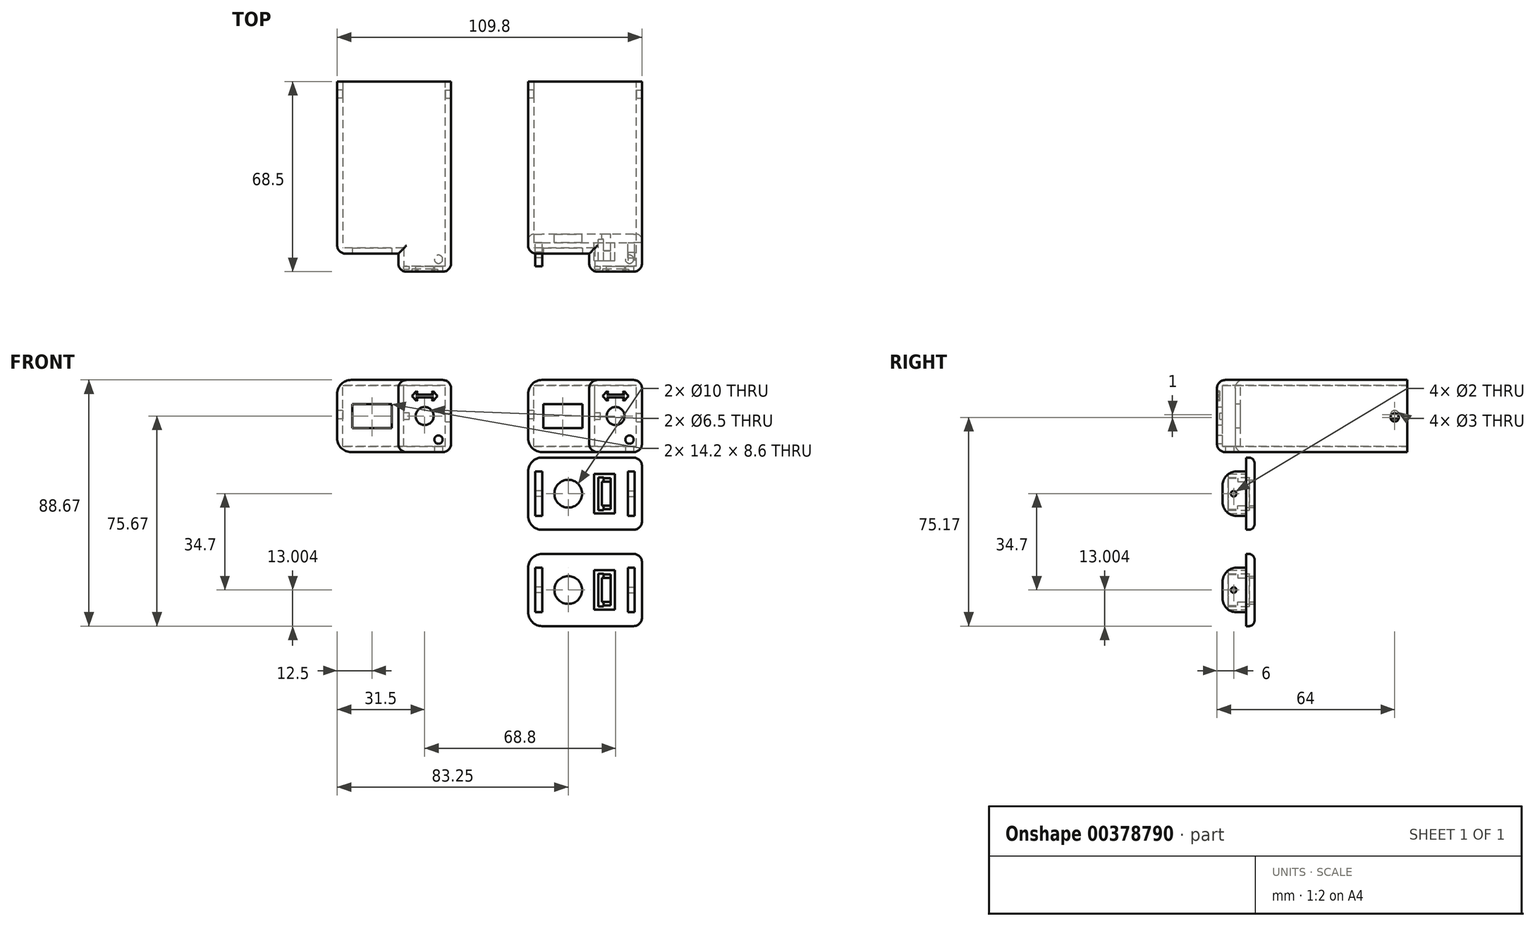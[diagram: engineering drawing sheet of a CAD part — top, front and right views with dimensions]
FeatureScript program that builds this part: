
annotation { "Feature Type Name" : "Feature", "Feature Type Description" : "" }
export const myFeature = defineFeature(function(context is Context, id is Id, definition is map)
    precondition{}
    {
        {
            var Q0;
            Q0=qCreatedBy(makeId("Front.planeOp"),FACE);
            var sketch = newSketch(context, id + "F0", { "sketchPlane" : qUnion([Q0])});
            skLineSegment(sketch, "E0.bottom", {"start": v(0, 0) * mm, "end": v(41, 0) * mm});
            skLineSegment(sketch, "E0.top", {"start": v(0, 26) * mm, "end": v(41, 26) * mm});
            skLineSegment(sketch, "E0.left", {"start": v(0, 0) * mm, "end": v(0, 26) * mm});
            skLineSegment(sketch, "E0.right", {"start": v(41, 0) * mm, "end": v(41, 26) * mm});
            skLineSegment(sketch, "E1.0", {"start": v(2, 2) * mm, "end": v(2, 24) * mm});
            skLineSegment(sketch, "E2.0", {"start": v(2, 24) * mm, "end": v(39, 24) * mm});
            skLineSegment(sketch, "E3.0", {"start": v(2, 2) * mm, "end": v(39, 2) * mm});
            skCircle(sketch, "E4", {"center": v(31.5, 13) * mm, "radius": 3.25 * mm});
            skCircle(sketch, "E5", {"center": v(31.5, 13) * mm, "radius": 4.5 * mm});
            skCircle(sketch, "E6", {"center": v(31.5, 13) * mm, "radius": 6 * mm});
            skPoint(sketch, "E7.endSnap0", {"position": v(20.5, 26) * mm});
            skLineSegment(sketch, "E8.0", {"start": v(0, 13) * mm, "end": v(40, 13) * mm, "construction": true});
            skLineSegment(sketch, "E9", {"start": v(0, -1.97) * mm, "end": v(41, -1.97) * mm});
            skLineSegment(sketch, "E10", {"start": v(41, -1.97) * mm, "end": v(41, -27.97) * mm});
            skLineSegment(sketch, "E11", {"start": v(41, -27.97) * mm, "end": v(0, -27.97) * mm});
            skLineSegment(sketch, "E12", {"start": v(0, -27.97) * mm, "end": v(0, -1.97) * mm});
            skLineSegment(sketch, "E13.0", {"start": v(2, -25.97) * mm, "end": v(2, -3.97) * mm});
            skLineSegment(sketch, "E13.1", {"start": v(39, -25.97) * mm, "end": v(2, -25.97) * mm});
            skLineSegment(sketch, "E13.2", {"start": v(39, -3.97) * mm, "end": v(39, -25.97) * mm});
            skLineSegment(sketch, "E13.3", {"start": v(2, -3.97) * mm, "end": v(39, -3.97) * mm});
            skLineSegment(sketch, "E14.0", {"start": v(2.6, -25.97) * mm, "end": v(2.6, -3.97) * mm});
            skLineSegment(sketch, "E15.0", {"start": v(38.4, -3.97) * mm, "end": v(38.4, -25.97) * mm});
            skLineSegment(sketch, "E16.0", {"start": v(5.1, -25.97) * mm, "end": v(5.1, -3.97) * mm});
            skLineSegment(sketch, "E17.0", {"start": v(35.9, -3.97) * mm, "end": v(35.9, -25.97) * mm});
            skLineSegment(sketch, "E18.0", {"start": v(20, -30) * mm, "end": v(20, -3.85) * mm, "construction": true});
            skLineSegment(sketch, "E19.0", {"start": v(27.5, -30) * mm, "end": v(27.5, -3.85) * mm, "construction": true});
            skLineSegment(sketch, "E20.0", {"start": v(14.45, -30) * mm, "end": v(14.45, -3.85) * mm, "construction": true});
            skCircle(sketch, "E21", {"center": v(14.45, -14.97) * mm, "radius": 6.5 * mm, "construction": true});
            skCircle(sketch, "E22", {"center": v(14.45, -14.97) * mm, "radius": 5 * mm});
            skLineSegment(sketch, "E23", {"start": v(25.3, -9.37) * mm, "end": v(25.3, -14.97) * mm});
            skLineSegment(sketch, "E24", {"start": v(23.8, -7.87) * mm, "end": v(31.2, -7.87) * mm});
            skLineSegment(sketch, "E25.MirrorCS", {"start": v(23.8, -22.07) * mm, "end": v(31.2, -22.07) * mm});
            skLineSegment(sketch, "E26", {"start": v(2.6, -24.97) * mm, "end": v(5.1, -24.97) * mm, "construction": true});
            skLineSegment(sketch, "E27", {"start": v(2.6, -4.97) * mm, "end": v(5.1, -4.97) * mm, "construction": true});
            skLineSegment(sketch, "E28", {"start": v(35.9, -4.97) * mm, "end": v(38.4, -4.97) * mm, "construction": true});
            skLineSegment(sketch, "E29", {"start": v(35.9, -24.97) * mm, "end": v(38.4, -24.97) * mm, "construction": true});
            skLineSegment(sketch, "E30.1", {"start": v(26.55, -9.37) * mm, "end": v(26.55, -14.97) * mm});
            skLineSegment(sketch, "E31.0", {"start": v(40, -14.97) * mm, "end": v(0, -14.97) * mm, "construction": true});
            skLineSegment(sketch, "E32.0", {"start": v(2.6, -6.97) * mm, "end": v(5.1, -6.97) * mm});
            skLineSegment(sketch, "E33.0", {"start": v(2.6, -22.97) * mm, "end": v(5.1, -22.97) * mm});
            skLineSegment(sketch, "E34.0", {"start": v(35.9, -22.97) * mm, "end": v(38.4, -22.97) * mm});
            skLineSegment(sketch, "E35.0", {"start": v(35.9, -6.97) * mm, "end": v(38.4, -6.97) * mm});
            skLineSegment(sketch, "E36", {"start": v(25.3, -9.37) * mm, "end": v(29.7, -9.37) * mm});
            skLineSegment(sketch, "E37", {"start": v(29.7, -9.37) * mm, "end": v(29.7, -14.97) * mm});
            skLineSegment(sketch, "E38", {"start": v(23.8, -7.87) * mm, "end": v(23.8, -22.07) * mm});
            skLineSegment(sketch, "E39", {"start": v(31.2, -22.07) * mm, "end": v(31.2, -7.87) * mm});
            skLineSegment(sketch, "E40", {"start": v(25.3, -9.37) * mm, "end": v(25.3, -9.07) * mm});
            skLineSegment(sketch, "E41", {"start": v(25.3, -9.07) * mm, "end": v(26.55, -9.07) * mm});
            skLineSegment(sketch, "E42", {"start": v(26.55, -9.07) * mm, "end": v(26.55, -9.37) * mm});
            skLineSegment(sketch, "E43", {"start": v(29.7, -10.67) * mm, "end": v(27.2, -10.67) * mm});
            skLineSegment(sketch, "E44", {"start": v(27.2, -10.67) * mm, "end": v(27.2, -9.37) * mm});
            skLineSegment(sketch, "E45.MirrorCS", {"start": v(40, -6.37) * mm, "end": v(0, -6.37) * mm, "construction": true});
            skLineSegment(sketch, "E46.MirrorCS", {"start": v(26.55, -20.87) * mm, "end": v(26.55, -20.57) * mm});
            skLineSegment(sketch, "E47.MirrorCS", {"start": v(25.3, -20.57) * mm, "end": v(25.3, -20.87) * mm});
            skLineSegment(sketch, "E48.MirrorCS", {"start": v(27.2, -19.27) * mm, "end": v(27.2, -20.57) * mm});
            skLineSegment(sketch, "E49.MirrorCS", {"start": v(25.3, -20.57) * mm, "end": v(25.3, -14.97) * mm});
            skLineSegment(sketch, "E50.MirrorCS", {"start": v(26.55, -20.57) * mm, "end": v(26.55, -14.97) * mm});
            skLineSegment(sketch, "E51.MirrorCS", {"start": v(27.5, 0.06) * mm, "end": v(27.5, -26.09) * mm, "construction": true});
            skLineSegment(sketch, "E52.MirrorCS", {"start": v(29.7, -19.27) * mm, "end": v(27.2, -19.27) * mm});
            skLineSegment(sketch, "E53.MirrorCS", {"start": v(25.3, -20.57) * mm, "end": v(29.7, -20.57) * mm});
            skLineSegment(sketch, "E54.MirrorCS", {"start": v(29.7, -20.57) * mm, "end": v(29.7, -14.97) * mm});
            skLineSegment(sketch, "E55.MirrorCS", {"start": v(25.3, -20.87) * mm, "end": v(26.55, -20.87) * mm});
            skLineSegment(sketch, "E56", {"start": v(27.2, -10.67) * mm, "end": v(26.55, -10.67) * mm});
            skLineSegment(sketch, "E57", {"start": v(27.2, -19.27) * mm, "end": v(26.55, -19.27) * mm});
            skLineSegment(sketch, "E58.0", {"start": v(39, 2) * mm, "end": v(39, 24) * mm});
            skLineSegment(sketch, "E59.0", {"start": v(22, 0) * mm, "end": v(22, 26) * mm});
            skLineSegment(sketch, "E60.0", {"start": v(24, 0) * mm, "end": v(24, 26) * mm, "construction": true});
            skLineSegment(sketch, "E61.0", {"start": v(31.5, 0) * mm, "end": v(31.5, 26) * mm, "construction": true});
            skSolve(sketch);
        }
        {
            var Q0;
            {var subQ0=sQuery(id+"F0.wireOp",EDGE,"163d6316-92f5-46fe-b325-45e71893f864.0");Q0=makeQuery(id+"F0.imprint","IMPRINT",FACE,{"disambiguationData":[TD([[makeQuery(id+"F0.imprint","IMPRINT",EDGE,{"derivedFrom":subQ0}),1.0]])]});}
            var Q1;
            Q1=makeQuery(id+"F0.imprint","IMPRINT",FACE,{"disambiguationData":[TD([[makeQuery(id+"F0.imprint","IMPRINT",EDGE,{"derivedFrom":sQuery(id+"F0.wireOp",EDGE,"E6")}),-1.0]])]});
            var Q2;
            {var subQ0=sQuery(id+"F0.wireOp",EDGE,"E0.right");Q2=makeQuery(id+"F0.imprint","IMPRINT",FACE,{"disambiguationData":[TD([[makeQuery(id+"F0.imprint","IMPRINT",EDGE,{"derivedFrom":subQ0}),1.0]])]});}
            extrude(context, id + "F1", {"entities" : qUnion([Q0, Q1, Q2]), "depth" : 13.5 * mm});
        }
        {
            var Q0;
            Q0=makeQuery(id+"F0.imprint","IMPRINT",FACE,{"disambiguationData":[TD([[makeQuery(id+"F0.imprint","IMPRINT",EDGE,{"derivedFrom":sQuery(id+"F0.wireOp",EDGE,"E4")}),-1.0]])]});
            var Q1;
            Q1=makeQuery(id+"F0.imprint","IMPRINT",FACE,{"disambiguationData":[TD([[makeQuery(id+"F0.imprint","IMPRINT",EDGE,{"derivedFrom":sQuery(id+"F0.wireOp",EDGE,"E5")}),-1.0]])]});
            extrude(context, id + "F2", {"entities" : qUnion([Q0, Q1]), "operationType" : NewBodyOperationType.ADD, "depth" : 13.5 * mm});
        }
        {
            var Q0;
            Q0=makeQuery(id+"F1.opExtrude","SWEPT_FACE",FACE,{"disambiguationData":[OSD([sQuery(id+"F0.wireOp",EDGE,"E59.0")])]});
            var sketch = newSketch(context, id + "F3", { "sketchPlane" : qUnion([Q0])});
            skLineSegment(sketch, "E62.0", {"start": v(13.5, 24) * mm, "end": v(0, 24) * mm});
            skLineSegment(sketch, "E63.0", {"start": v(13.5, 2) * mm, "end": v(0, 2) * mm});
            skLineSegment(sketch, "E64.0", {"start": v(11.5, 0) * mm, "end": v(11.5, 26) * mm});
            skSolve(sketch);
        }
        {
            var Q0;
            {var subQ0=sQuery(id+"F3.wireOp",EDGE,"E62.0");var subQ1=makeQuery(id+"F1.opExtrude","CAP_EDGE",EDGE,{"disambiguationData":[OSD([sQuery(id+"F0.wireOp",EDGE,"E59.0")])],"isStart":true});var subQ2=makeQuery(id+"F3.imprint","INTERSECT",VERTEX,{"derivedFrom":[subQ1,subQ0]});Q0=makeQuery(id+"F3.imprint","IMPRINT",FACE,{"disambiguationData":[TD([[makeQuery(id+"F3.imprint","IMPRINT",EDGE,{"disambiguationData":[TD([[subQ2,1.0]])],"derivedFrom":subQ0}),1.0]])]});}
            extrude(context, id + "F4", {"entities" : qUnion([Q0]), "operationType" : NewBodyOperationType.REMOVE, "oppositeDirection" : true, "depth" : 17 * mm});
        }
        {
            var Q0;
            Q0=makeQuery(id+"F4.boolean.opBoolean","COPY",FACE,{"derivedFrom":makeQuery(id+"F4.opExtrude","SWEPT_FACE",FACE,{"disambiguationData":[OSD([sQuery(id+"F3.wireOp",EDGE,"E64.0")])]})});
            var sketch = newSketch(context, id + "F5", { "sketchPlane" : qUnion([Q0])});
            skLineSegment(sketch, "E65.0", {"start": v(-24, 2) * mm, "end": v(-24, 24) * mm});
            skSolve(sketch);
        }
        {
            var Q0;
            {var subQ0=sQuery(id+"F5.wireOp",EDGE,"E65.0");Q0=makeQuery(id+"F5.imprint","IMPRINT",FACE,{"disambiguationData":[TD([[makeQuery(id+"F5.imprint","IMPRINT",EDGE,{"derivedFrom":subQ0}),-1.0]])]});}
            extrude(context, id + "F6", {"entities" : qUnion([Q0]), "operationType" : NewBodyOperationType.ADD, "depth" : 6.5 * mm});
        }
        {
            var Q0;
            Q0=makeQuery(id+"F6.boolean.opBoolean","MERGE",FACE,{"derivedFrom":[makeQuery(id+"F1.opExtrude","SWEPT_FACE",FACE,{"disambiguationData":[OSD([sQuery(id+"F0.wireOp",EDGE,"E59.0")])]}),makeQuery(id+"F6.opExtrude","SWEPT_FACE",FACE,{"disambiguationData":[OSD([sQuery(id+"F3.wireOp",EDGE,"E64.0")])]})]});
            var sketch = newSketch(context, id + "F7", { "sketchPlane" : qUnion([Q0])});
            skLineSegment(sketch, "E66", {"start": v(5, 24) * mm, "end": v(5, 26) * mm});
            skLineSegment(sketch, "E67", {"start": v(5, 2) * mm, "end": v(5, 0) * mm});
            skLineSegment(sketch, "E68.0", {"start": v(7, 24) * mm, "end": v(7, 26) * mm});
            skLineSegment(sketch, "E68.1", {"start": v(7, 2) * mm, "end": v(7, 24) * mm});
            skLineSegment(sketch, "E68.2", {"start": v(7, 2) * mm, "end": v(7, 0) * mm});
            skSolve(sketch);
        }
        {
            var Q0;
            {var subQ5=sQuery(id+"F7.wireOp",EDGE,"E66");Q0=makeQuery(id+"F7.imprint","IMPRINT",FACE,{"disambiguationData":[TD([[makeQuery(id+"F7.imprint","IMPRINT",EDGE,{"derivedFrom":subQ5}),-1.0]])]});}
            var Q1;
            {var subQ0=sQuery(id+"F7.wireOp",EDGE,"E67");Q1=makeQuery(id+"F7.imprint","IMPRINT",FACE,{"disambiguationData":[TD([[makeQuery(id+"F7.imprint","IMPRINT",EDGE,{"derivedFrom":subQ0}),-1.0]])]});}
            var Q2;
            {var subQ0=sQuery(id+"F7.wireOp",EDGE,"E66");Q2=makeQuery(id+"F7.imprint","IMPRINT",FACE,{"disambiguationData":[TD([[makeQuery(id+"F7.imprint","IMPRINT",EDGE,{"derivedFrom":subQ0}),1.0]])]});}
            var Q3;
            Q3 = qSketchRegion(id + "F9", true);
            extrude(context, id + "F8", {"entities" : qUnion([Q0, Q1, Q2, Q3]), "operationType" : NewBodyOperationType.ADD, "depth" : 22 * mm});
        }
        {
            var Q0;
            Q0=makeQuery(id+"F8.opExtrude","SWEPT_FACE",FACE,{"disambiguationData":[OSD([sQuery(id+"F7.wireOp",EDGE,"E68.0"),sQuery(id+"F7.wireOp",EDGE,"E68.1"),sQuery(id+"F7.wireOp",EDGE,"E68.2")])]});
            var sketch = newSketch(context, id + "F9", { "sketchPlane" : qUnion([Q0])});
            skLineSegment(sketch, "E69.0", {"start": v(0, 13) * mm, "end": v(41, 13) * mm, "construction": true});
            skLineSegment(sketch, "E70.0", {"start": v(12.5, 0) * mm, "end": v(12.5, 26) * mm, "construction": true});
            skLineSegment(sketch, "E71", {"start": v(12.5, 17.3) * mm, "end": v(19.6, 17.3) * mm});
            skLineSegment(sketch, "E72", {"start": v(19.6, 17.3) * mm, "end": v(19.6, 13) * mm});
            skLineSegment(sketch, "E73.MirrorCS", {"start": v(5.4, 17.3) * mm, "end": v(5.4, 13) * mm});
            skLineSegment(sketch, "E74.MirrorCS", {"start": v(12.5, 17.3) * mm, "end": v(5.4, 17.3) * mm});
            skLineSegment(sketch, "E75.MirrorCS", {"start": v(19.6, 8.7) * mm, "end": v(19.6, 13) * mm});
            skLineSegment(sketch, "E76.MirrorCS", {"start": v(12.5, 8.7) * mm, "end": v(19.6, 8.7) * mm});
            skLineSegment(sketch, "E77.MirrorCS", {"start": v(5.4, 8.7) * mm, "end": v(5.4, 13) * mm});
            skLineSegment(sketch, "E78.MirrorCS", {"start": v(12.5, 8.7) * mm, "end": v(5.4, 8.7) * mm});
            skSolve(sketch);
        }
        {
            var Q0;
            Q0=makeQuery(id+"F9.imprint","IMPRINT",FACE,{"disambiguationData":[TD([[makeQuery(id+"F9.imprint","IMPRINT",EDGE,{"derivedFrom":sQuery(id+"F9.wireOp",EDGE,"eaKKzyx9-IUk8-CNGP-EQG6-oQ9AtWCfZGGG")}),-1.0]])]});
            var Q1;
            Q1=makeQuery(id+"F9.imprint","IMPRINT",FACE,{"disambiguationData":[TD([[makeQuery(id+"F9.imprint","IMPRINT",EDGE,{"derivedFrom":sQuery(id+"F9.wireOp",EDGE,"E71")}),-1.0]])]});
            extrude(context, id + "F10", {"entities" : qUnion([Q0, Q1]), "operationType" : NewBodyOperationType.REMOVE, "oppositeDirection" : true, "depth" : 2 * mm});
        }
        {
            var Q0;
            {var subQ1=sQuery(id+"F0.wireOp",EDGE,"E0.left");Q0=makeQuery(id+"F0.imprint","IMPRINT",FACE,{"disambiguationData":[TD([[makeQuery(id+"F0.imprint","IMPRINT",EDGE,{"derivedFrom":subQ1}),-1.0]])]});}
            var Q1;
            {var subQ3=sQuery(id+"F0.wireOp",EDGE,"163d6316-92f5-46fe-b325-45e71893f864.0");Q1=makeQuery(id+"F0.imprint","IMPRINT",FACE,{"disambiguationData":[TD([[makeQuery(id+"F0.imprint","IMPRINT",EDGE,{"derivedFrom":subQ3}),-1.0]])]});}
            var Q2;
            {var subQ0=sQuery(id+"F0.wireOp",EDGE,"E7");var subQ1=sQuery(id+"F0.wireOp",EDGE,"E0.top");var subQ2=makeQuery(id+"F0.imprint","INTERSECT",VERTEX,{"derivedFrom":[subQ1,subQ0]});Q2=makeQuery(id+"F0.imprint","IMPRINT",FACE,{"disambiguationData":[TD([[makeQuery(id+"F0.imprint","IMPRINT",EDGE,{"disambiguationData":[TD([[subQ2,-1.0]])],"derivedFrom":subQ1}),-1.0]])]});}
            var Q3;
            {var subQ3=sQuery(id+"F0.wireOp",EDGE,"gIGV9JjZ-nNWi-Sog9-6HsN-JS0wgbCRWOlJ");Q3=makeQuery(id+"F0.imprint","IMPRINT",FACE,{"disambiguationData":[TD([[makeQuery(id+"F0.imprint","IMPRINT",EDGE,{"derivedFrom":subQ3}),1.0]])]});}
            extrude(context, id + "F11", {"entities" : qUnion([Q0, Q1, Q2, Q3]), "operationType" : NewBodyOperationType.ADD, "oppositeDirection" : true, "depth" : 55 * mm});
        }
        {
            var Q0;
            {var subQ0=sQuery(id+"F0.wireOp",EDGE,"E0.right");Q0=makeQuery(id+"F11.boolean.opBoolean","MERGE",FACE,{"derivedFrom":[makeQuery(id+"F1.opExtrude","SWEPT_FACE",FACE,{"disambiguationData":[OSD([subQ0])]}),makeQuery(id+"F11.opExtrude","SWEPT_FACE",FACE,{"disambiguationData":[OSD([subQ0])]})]});}
            var sketch = newSketch(context, id + "F12", { "sketchPlane" : qUnion([Q0])});
            skLineSegment(sketch, "E79.0", {"start": v(50.5, 0) * mm, "end": v(50.5, 25) * mm, "construction": true});
            skLineSegment(sketch, "E80.0", {"start": v(-13.5, 12.5) * mm, "end": v(50, 12.5) * mm, "construction": true});
            skCircle(sketch, "E81", {"center": v(50.5, 12.5) * mm, "radius": 1.5 * mm});
            skLineSegment(sketch, "E82.0", {"start": v(50, 0) * mm, "end": v(50, 22) * mm, "construction": true});
            skSolve(sketch);
        }
        {
            var Q0;
            Q0=makeQuery(id+"F12.imprint","IMPRINT",FACE,{"disambiguationData":[TD([[makeQuery(id+"F12.imprint","IMPRINT",EDGE,{"derivedFrom":sQuery(id+"F12.wireOp",EDGE,"E81")}),1.0]])]});
            var Q1;
            Q1=sQuery(id+"F12.wireOp",EDGE,"E81");
            extrude(context, id + "F13", {"entities" : qUnion([Q0]), "operationType" : NewBodyOperationType.REMOVE, "surfaceEntities" : qUnion([Q1]), "oppositeDirection" : true, "depth" : 2 * mm});
        }
        {
            var Q0;
            {var subQ0=sQuery(id+"F3.wireOp",EDGE,"08461534-4a8e-414f-8055-8d0c99b7fd05.0");Q0=makeQuery(id+"F11.boolean.opBoolean","MERGE",FACE,{"derivedFrom":[makeQuery(id+"F5sBlkcHSTYC5dn_1.boolean.opBoolean","MERGE",FACE,{"derivedFrom":[makeQuery(id+"F8.opExtrude","CAP_FACE",FACE,{"disambiguationData":[OSD([sQuery(id+"F0.wireOp",EDGE,"E0.bottom"),sQuery(id+"F0.wireOp",EDGE,"E0.top"),sQuery(id+"F0.wireOp",EDGE,"E7"),sQuery(id+"F0.wireOp",EDGE,"gIGV9JjZ-nNWi-Sog9-6HsN-JS0wgbCRWOlJ"),sQuery(id+"F3.wireOp",EDGE,"09efee87-d6d9-4323-927c-8563ffcb2ae2.0"),subQ0,sQuery(id+"F3.wireOp",EDGE,"08750dff-402c-4c7d-b57e-c4fba2cf869d.0"),sQuery(id+"F7.wireOp",EDGE,"50574ae9-b3cd-46b7-9d75-bf72c58a5bcf.0"),sQuery(id+"F7.wireOp",EDGE,"SYQ2j7Xk-EsEA-CMjw-MBcL-rHaNIxYhDTL1"),sQuery(id+"F7.wireOp",EDGE,"9hsKS0mZ-jZcg-CKVl-3s8W-167S1Uym6Gdj")])],"isStart":false}),makeQuery(id+"F5sBlkcHSTYC5dn_1.opExtrude","SWEPT_FACE",FACE,{"disambiguationData":[OSD([subQ0])]})]}),makeQuery(id+"F11.opExtrude","SWEPT_FACE",FACE,{"disambiguationData":[OSD([sQuery(id+"F0.wireOp",EDGE,"E0.left")])]})]});}
            var sketch = newSketch(context, id + "F14", { "sketchPlane" : qUnion([Q0])});
            skLineSegment(sketch, "E83.0", {"start": v(-50.5, 0) * mm, "end": v(-50.5, 27) * mm, "construction": true});
            skLineSegment(sketch, "E84.0", {"start": v(-48, 0) * mm, "end": v(-48, 26) * mm, "construction": true});
            skLineSegment(sketch, "E85.0", {"start": v(8, 13.5) * mm, "end": v(-50, 13.5) * mm, "construction": true});
            skCircle(sketch, "E86", {"center": v(-50.5, 13.5) * mm, "radius": 1.5 * mm});
            skSolve(sketch);
        }
        {
            var Q0;
            Q0=makeQuery(id+"F14.imprint","IMPRINT",FACE,{"disambiguationData":[TD([[makeQuery(id+"F14.imprint","IMPRINT",EDGE,{"derivedFrom":sQuery(id+"F14.wireOp",EDGE,"E86")}),1.0]])]});
            extrude(context, id + "F15", {"entities" : qUnion([Q0]), "operationType" : NewBodyOperationType.REMOVE, "oppositeDirection" : true, "depth" : 2 * mm});
        }
        {
            var Q0;
            Q0=makeQuery(id+"F4.boolean.opBoolean","COPY",FACE,{"derivedFrom":makeQuery(id+"F4.opExtrude","SWEPT_FACE",FACE,{"disambiguationData":[OSD([sQuery(id+"F3.wireOp",EDGE,"E64.0")])]})});
            var sketch = newSketch(context, id + "F16", { "sketchPlane" : qUnion([Q0])});
            skLineSegment(sketch, "E87.0", {"start": v(-39, 13) * mm, "end": v(-24, 13) * mm, "construction": true});
            skLineSegment(sketch, "E88.0", {"start": v(-39, 11.9) * mm, "end": v(-24, 11.9) * mm, "construction": true});
            skLineSegment(sketch, "E89.0", {"start": v(-39, 14.1) * mm, "end": v(-24, 14.1) * mm, "construction": true});
            skLineSegment(sketch, "E90.0", {"start": v(-26, 2) * mm, "end": v(-26, 24) * mm, "construction": true});
            skLineSegment(sketch, "E91", {"start": v(-24, 11.9) * mm, "end": v(-26, 11.9) * mm});
            skLineSegment(sketch, "E92", {"start": v(-26, 11.9) * mm, "end": v(-26, 14.1) * mm});
            skLineSegment(sketch, "E93", {"start": v(-26, 14.1) * mm, "end": v(-24, 14.1) * mm});
            skSolve(sketch);
        }
        {
            var Q0;
            {var subQ0=sQuery(id+"F16.wireOp",EDGE,"E91");Q0=makeQuery(id+"F16.imprint","IMPRINT",FACE,{"disambiguationData":[TD([[makeQuery(id+"F16.imprint","IMPRINT",EDGE,{"derivedFrom":subQ0}),-1.0]])]});}
            extrude(context, id + "F17", {"entities" : qUnion([Q0]), "operationType" : NewBodyOperationType.REMOVE, "oppositeDirection" : true, "depth" : 1 * mm});
        }
        {
            var Q0;
            Q0=makeQuery(id+"F0.imprint","IMPRINT",FACE,{"disambiguationData":[TD([[makeQuery(id+"F0.imprint","IMPRINT",EDGE,{"derivedFrom":sQuery(id+"F0.wireOp",EDGE,"E9")}),-1.0]])]});
            var Q1;
            {var subQ0=sQuery(id+"F0.wireOp",EDGE,"3f6121a4-fa6f-475a-9cc1-ae866b2f2f2d.0");var subQ1=sQuery(id+"F0.wireOp",EDGE,"E13.0");var subQ2=makeQuery(id+"F0.imprint","INTERSECT",VERTEX,{"derivedFrom":[subQ1,subQ0]});Q1=makeQuery(id+"F0.imprint","IMPRINT",FACE,{"disambiguationData":[TD([[makeQuery(id+"F0.imprint","IMPRINT",EDGE,{"disambiguationData":[TD([[subQ2,-1.0]])],"derivedFrom":subQ1}),-1.0]])]});}
            var Q2;
            {var subQ0=sQuery(id+"F0.wireOp",EDGE,"E13.3");var subQ1=sQuery(id+"F0.wireOp",EDGE,"E13.0");var subQ2=makeQuery(id+"F0.imprint","INTERSECT",VERTEX,{"derivedFrom":[subQ1,subQ0]});Q2=makeQuery(id+"F0.imprint","IMPRINT",FACE,{"disambiguationData":[TD([[makeQuery(id+"F0.imprint","IMPRINT",EDGE,{"disambiguationData":[TD([[subQ2,1.0]])],"derivedFrom":subQ1}),-1.0]])]});}
            var Q3;
            {var subQ0=sQuery(id+"F0.wireOp",EDGE,"E14.0");var subQ1=sQuery(id+"F0.wireOp",EDGE,"E13.3");var subQ2=makeQuery(id+"F0.imprint","INTERSECT",VERTEX,{"derivedFrom":[subQ1,subQ0]});Q3=makeQuery(id+"F0.imprint","IMPRINT",FACE,{"disambiguationData":[TD([[makeQuery(id+"F0.imprint","IMPRINT",EDGE,{"disambiguationData":[TD([[subQ2,-1.0]])],"derivedFrom":subQ1}),-1.0]])]});}
            var Q4;
            {var subQ0=sQuery(id+"F0.wireOp",EDGE,"E16.0");var subQ1=sQuery(id+"F0.wireOp",EDGE,"E13.3");var subQ2=makeQuery(id+"F0.imprint","INTERSECT",VERTEX,{"derivedFrom":[subQ1,subQ0]});Q4=makeQuery(id+"F0.imprint","IMPRINT",FACE,{"disambiguationData":[TD([[makeQuery(id+"F0.imprint","IMPRINT",EDGE,{"disambiguationData":[TD([[subQ2,-1.0]])],"derivedFrom":subQ1}),-1.0]])]});}
            var Q5;
            {var subQ0=sQuery(id+"F0.wireOp",EDGE,"E13.1");var subQ1=sQuery(id+"F0.wireOp",EDGE,"E13.0");var subQ2=makeQuery(id+"F0.imprint","INTERSECT",VERTEX,{"derivedFrom":[subQ1,subQ0]});Q5=makeQuery(id+"F0.imprint","IMPRINT",FACE,{"disambiguationData":[TD([[makeQuery(id+"F0.imprint","IMPRINT",EDGE,{"disambiguationData":[TD([[subQ2,-1.0]])],"derivedFrom":subQ1}),-1.0]])]});}
            var Q6;
            {var subQ0=sQuery(id+"F0.wireOp",EDGE,"E14.0");var subQ1=sQuery(id+"F0.wireOp",EDGE,"E13.1");var subQ2=makeQuery(id+"F0.imprint","INTERSECT",VERTEX,{"derivedFrom":[subQ1,subQ0]});Q6=makeQuery(id+"F0.imprint","IMPRINT",FACE,{"disambiguationData":[TD([[makeQuery(id+"F0.imprint","IMPRINT",EDGE,{"disambiguationData":[TD([[subQ2,1.0]])],"derivedFrom":subQ1}),-1.0]])]});}
            var Q7;
            {var subQ0=sQuery(id+"F0.wireOp",EDGE,"E17.0");var subQ1=sQuery(id+"F0.wireOp",EDGE,"3f6121a4-fa6f-475a-9cc1-ae866b2f2f2d.0");var subQ2=makeQuery(id+"F0.imprint","INTERSECT",VERTEX,{"derivedFrom":[subQ1,subQ0]});Q7=makeQuery(id+"F0.imprint","IMPRINT",FACE,{"disambiguationData":[TD([[makeQuery(id+"F0.imprint","IMPRINT",EDGE,{"disambiguationData":[TD([[subQ2,-1.0]])],"derivedFrom":subQ1}),-1.0]])]});}
            var Q8;
            {var subQ0=sQuery(id+"F0.wireOp",EDGE,"E15.0");var subQ1=sQuery(id+"F0.wireOp",EDGE,"E13.3");var subQ2=makeQuery(id+"F0.imprint","INTERSECT",VERTEX,{"derivedFrom":[subQ1,subQ0]});Q8=makeQuery(id+"F0.imprint","IMPRINT",FACE,{"disambiguationData":[TD([[makeQuery(id+"F0.imprint","IMPRINT",EDGE,{"disambiguationData":[TD([[subQ2,1.0]])],"derivedFrom":subQ1}),-1.0]])]});}
            var Q9;
            {var subQ0=sQuery(id+"F0.wireOp",EDGE,"E13.3");var subQ1=sQuery(id+"F0.wireOp",EDGE,"E13.2");var subQ2=makeQuery(id+"F0.imprint","INTERSECT",VERTEX,{"derivedFrom":[subQ1,subQ0]});Q9=makeQuery(id+"F0.imprint","IMPRINT",FACE,{"disambiguationData":[TD([[makeQuery(id+"F0.imprint","IMPRINT",EDGE,{"disambiguationData":[TD([[subQ2,-1.0]])],"derivedFrom":subQ1}),-1.0]])]});}
            var Q10;
            {var subQ0=sQuery(id+"F0.wireOp",EDGE,"3f6121a4-fa6f-475a-9cc1-ae866b2f2f2d.0");var subQ1=sQuery(id+"F0.wireOp",EDGE,"E13.2");var subQ2=makeQuery(id+"F0.imprint","INTERSECT",VERTEX,{"derivedFrom":[subQ1,subQ0]});Q10=makeQuery(id+"F0.imprint","IMPRINT",FACE,{"disambiguationData":[TD([[makeQuery(id+"F0.imprint","IMPRINT",EDGE,{"disambiguationData":[TD([[subQ2,1.0]])],"derivedFrom":subQ1}),-1.0]])]});}
            var Q11;
            {var subQ0=sQuery(id+"F0.wireOp",EDGE,"E13.2");var subQ1=sQuery(id+"F0.wireOp",EDGE,"E13.1");var subQ2=makeQuery(id+"F0.imprint","INTERSECT",VERTEX,{"derivedFrom":[subQ1,subQ0]});Q11=makeQuery(id+"F0.imprint","IMPRINT",FACE,{"disambiguationData":[TD([[makeQuery(id+"F0.imprint","IMPRINT",EDGE,{"disambiguationData":[TD([[subQ2,-1.0]])],"derivedFrom":subQ1}),-1.0]])]});}
            var Q12;
            {var subQ0=sQuery(id+"F0.wireOp",EDGE,"E15.0");var subQ1=sQuery(id+"F0.wireOp",EDGE,"E13.1");var subQ2=makeQuery(id+"F0.imprint","INTERSECT",VERTEX,{"derivedFrom":[subQ1,subQ0]});Q12=makeQuery(id+"F0.imprint","IMPRINT",FACE,{"disambiguationData":[TD([[makeQuery(id+"F0.imprint","IMPRINT",EDGE,{"disambiguationData":[TD([[subQ2,-1.0]])],"derivedFrom":subQ1}),-1.0]])]});}
            extrude(context, id + "F18", {"entities" : qUnion([Q0, Q1, Q2, Q3, Q4, Q5, Q6, Q7, Q8, Q9, Q10, Q11, Q12]), "depth" : 3 * mm});
        }
        {
            var Q0;
            {var subQ0=sQuery(id+"F0.wireOp",EDGE,"E26");Q0=makeQuery(id+"F0.imprint","IMPRINT",FACE,{"disambiguationData":[TD([[makeQuery(id+"F0.imprint","IMPRINT",EDGE,{"derivedFrom":subQ0}),1.0]])]});}
            var Q1;
            {var subQ0=sQuery(id+"F0.wireOp",EDGE,"E28");Q1=makeQuery(id+"F0.imprint","IMPRINT",FACE,{"disambiguationData":[TD([[makeQuery(id+"F0.imprint","IMPRINT",EDGE,{"derivedFrom":subQ0}),-1.0]])]});}
            var Q2;
            {var subQ0=sQuery(id+"F0.wireOp",EDGE,"E32.0");Q2=makeQuery(id+"F0.imprint","IMPRINT",FACE,{"disambiguationData":[TD([[makeQuery(id+"F0.imprint","IMPRINT",EDGE,{"derivedFrom":subQ0}),-1.0]])]});}
            var Q3;
            {var subQ0=sQuery(id+"F0.wireOp",EDGE,"E34.0");Q3=makeQuery(id+"F0.imprint","IMPRINT",FACE,{"disambiguationData":[TD([[makeQuery(id+"F0.imprint","IMPRINT",EDGE,{"derivedFrom":subQ0}),1.0]])]});}
            extrude(context, id + "F19", {"entities" : qUnion([Q0, Q1, Q2, Q3]), "operationType" : NewBodyOperationType.ADD, "depth" : 11.5 * mm});
        }
        {
            var Q0;
            Q0=makeQuery(id+"F19.opExtrude","SWEPT_FACE",FACE,{"disambiguationData":[OSD([sQuery(id+"F0.wireOp",EDGE,"E14.0")])]});
            var sketch = newSketch(context, id + "F20", { "sketchPlane" : qUnion([Q0])});
            skLineSegment(sketch, "E94.0", {"start": v(19.5, -14.97) * mm, "end": v(-4.5, -14.97) * mm, "construction": true});
            skLineSegment(sketch, "E95.0", {"start": v(7.5, -28.66) * mm, "end": v(7.5, -1.27) * mm, "construction": true});
            skCircle(sketch, "E96", {"center": v(7.5, -14.97) * mm, "radius": 1 * mm});
            skSolve(sketch);
        }
        {
            var Q0;
            Q0=makeQuery(id+"F20.imprint","IMPRINT",FACE,{"disambiguationData":[TD([[makeQuery(id+"F20.imprint","IMPRINT",EDGE,{"derivedFrom":sQuery(id+"F20.wireOp",EDGE,"E96")}),1.0]])]});
            var Q1;
            Q1 = qSketchRegion(id + "F22", true);
            extrude(context, id + "F21", {"entities" : qUnion([Q0, Q1]), "operationType" : NewBodyOperationType.REMOVE, "oppositeDirection" : true, "depth" : 2.5 * mm});
        }
        {
            var Q0;
            Q0=makeQuery(id+"F19.opExtrude","SWEPT_FACE",FACE,{"disambiguationData":[OSD([sQuery(id+"F0.wireOp",EDGE,"E15.0")])]});
            var sketch = newSketch(context, id + "F22", { "sketchPlane" : qUnion([Q0])});
            skLineSegment(sketch, "E97.0", {"start": v(-7.5, -14.97) * mm, "end": v(-7.5, -14.97) * mm});
            skLineSegment(sketch, "E98.0", {"start": v(-7.5, -4.37) * mm, "end": v(-7.5, -25.57) * mm, "construction": true});
            skCircle(sketch, "E99", {"center": v(-7.5, -14.97) * mm, "radius": 1 * mm});
            skSolve(sketch);
        }
        {
            var Q0;
            Q0=qSketchRegion(id+"F22",true);
            extrude(context, id + "F23", {"entities" : qUnion([Q0]), "operationType" : NewBodyOperationType.REMOVE, "oppositeDirection" : true, "depth" : 2.5 * mm});
        }
        {
            var Q0;
            Q0=makeQuery(id+"F18.opExtrude","SWEPT_EDGE",EDGE,{"disambiguationData":[OSD([sQuery(id+"F0.wireOp",EDGE,"E11"),sQuery(id+"F0.wireOp",EDGE,"E12")])]});
            var Q1;
            Q1=makeQuery(id+"F18.opExtrude","SWEPT_EDGE",EDGE,{"disambiguationData":[OSD([sQuery(id+"F0.wireOp",EDGE,"E9"),sQuery(id+"F0.wireOp",EDGE,"E12")])]});
            fillet(context, id + "F24", {"entities" : qUnion([Q0, Q1]), "radius" : 5 * mm, "tangentPropagation" : true, "allowEdgeOverflow" : false});
        }
        {
            var Q0;
            Q0=makeQuery(id+"F18.opExtrude","SWEPT_EDGE",EDGE,{"disambiguationData":[OSD([sQuery(id+"F0.wireOp",EDGE,"E10"),sQuery(id+"F0.wireOp",EDGE,"E11")])]});
            var Q1;
            Q1=makeQuery(id+"F18.opExtrude","SWEPT_EDGE",EDGE,{"disambiguationData":[OSD([sQuery(id+"F0.wireOp",EDGE,"E9"),sQuery(id+"F0.wireOp",EDGE,"E10")])]});
            fillet(context, id + "F25", {"entities" : qUnion([Q0, Q1]), "radius" : 3 * mm, "tangentPropagation" : true, "allowEdgeOverflow" : false});
        }
        {
            var Q0;
            Q0=makeQuery(id+"F18.opExtrude","CAP_EDGE",EDGE,{"disambiguationData":[OSD([sQuery(id+"F0.wireOp",EDGE,"E11")])],"isStart":true});
            fillet(context, id + "F26", {"entities" : qUnion([Q0]), "radius" : 2 * mm, "tangentPropagation" : true, "allowEdgeOverflow" : false});
        }
        {
            var Q0;
            {var subQ0=sQuery(id+"F0.wireOp",EDGE,"cf0389e6-104e-45a0-a789-3107d1235b38.0");Q0=makeQuery(id+"F19.opExtrude","CAP_EDGE",EDGE,{"disambiguationData":[OSD([subQ0]),TDD([makeQuery(id+"F0.imprint","IMPRINT",EDGE,{"disambiguationData":[TD([[makeQuery(id+"F0.imprint","INTERSECT",VERTEX,{"derivedFrom":[sQuery(id+"F0.wireOp",EDGE,"E14.0"),subQ0]}),-1.0]])],"derivedFrom":subQ0})])],"isStart":false});}
            var Q1;
            {var subQ0=sQuery(id+"F0.wireOp",EDGE,"3f6121a4-fa6f-475a-9cc1-ae866b2f2f2d.0");Q1=makeQuery(id+"F19.opExtrude","CAP_EDGE",EDGE,{"disambiguationData":[OSD([subQ0]),TDD([makeQuery(id+"F0.imprint","IMPRINT",EDGE,{"disambiguationData":[TD([[makeQuery(id+"F0.imprint","INTERSECT",VERTEX,{"derivedFrom":[sQuery(id+"F0.wireOp",EDGE,"E14.0"),subQ0]}),1.0]])],"derivedFrom":subQ0})])],"isStart":false});}
            var Q2;
            {var subQ0=sQuery(id+"F0.wireOp",EDGE,"3f6121a4-fa6f-475a-9cc1-ae866b2f2f2d.0");Q2=makeQuery(id+"F19.opExtrude","CAP_EDGE",EDGE,{"disambiguationData":[OSD([subQ0]),TDD([makeQuery(id+"F0.imprint","IMPRINT",EDGE,{"disambiguationData":[TD([[makeQuery(id+"F0.imprint","INTERSECT",VERTEX,{"derivedFrom":[sQuery(id+"F0.wireOp",EDGE,"E15.0"),subQ0]}),-1.0]])],"derivedFrom":subQ0})])],"isStart":false});}
            var Q3;
            {var subQ0=sQuery(id+"F0.wireOp",EDGE,"cf0389e6-104e-45a0-a789-3107d1235b38.0");Q3=makeQuery(id+"F19.opExtrude","CAP_EDGE",EDGE,{"disambiguationData":[OSD([subQ0]),TDD([makeQuery(id+"F0.imprint","IMPRINT",EDGE,{"disambiguationData":[TD([[makeQuery(id+"F0.imprint","INTERSECT",VERTEX,{"derivedFrom":[sQuery(id+"F0.wireOp",EDGE,"E15.0"),subQ0]}),1.0]])],"derivedFrom":subQ0})])],"isStart":false});}
            var Q4;
            {var subQ0=sQuery(id+"F0.wireOp",EDGE,"E13.1");Q4=makeQuery(id+"F19.opExtrude","CAP_EDGE",EDGE,{"disambiguationData":[OSD([subQ0]),TDD([makeQuery(id+"F0.imprint","IMPRINT",EDGE,{"disambiguationData":[TD([[makeQuery(id+"F0.imprint","INTERSECT",VERTEX,{"derivedFrom":[subQ0,sQuery(id+"F0.wireOp",EDGE,"E14.0")]}),1.0]])],"derivedFrom":subQ0})])],"isStart":false});}
            var Q5;
            {var subQ0=sQuery(id+"F0.wireOp",EDGE,"E13.3");Q5=makeQuery(id+"F19.opExtrude","CAP_EDGE",EDGE,{"disambiguationData":[OSD([subQ0]),TDD([makeQuery(id+"F0.imprint","IMPRINT",EDGE,{"disambiguationData":[TD([[makeQuery(id+"F0.imprint","INTERSECT",VERTEX,{"derivedFrom":[subQ0,sQuery(id+"F0.wireOp",EDGE,"E14.0")]}),-1.0]])],"derivedFrom":subQ0})])],"isStart":false});}
            var Q6;
            {var subQ0=sQuery(id+"F0.wireOp",EDGE,"E13.3");Q6=makeQuery(id+"F19.opExtrude","CAP_EDGE",EDGE,{"disambiguationData":[OSD([subQ0]),TDD([makeQuery(id+"F0.imprint","IMPRINT",EDGE,{"disambiguationData":[TD([[makeQuery(id+"F0.imprint","INTERSECT",VERTEX,{"derivedFrom":[subQ0,sQuery(id+"F0.wireOp",EDGE,"E15.0")]}),1.0]])],"derivedFrom":subQ0})])],"isStart":false});}
            var Q7;
            {var subQ0=sQuery(id+"F0.wireOp",EDGE,"E13.1");Q7=makeQuery(id+"F19.opExtrude","CAP_EDGE",EDGE,{"disambiguationData":[OSD([subQ0]),TDD([makeQuery(id+"F0.imprint","IMPRINT",EDGE,{"disambiguationData":[TD([[makeQuery(id+"F0.imprint","INTERSECT",VERTEX,{"derivedFrom":[subQ0,sQuery(id+"F0.wireOp",EDGE,"E15.0")]}),-1.0]])],"derivedFrom":subQ0})])],"isStart":false});}
            var Q8;
            Q8=makeQuery(id+"F19.opExtrude","CAP_EDGE",EDGE,{"disambiguationData":[OSD([sQuery(id+"F0.wireOp",EDGE,"E26")])],"isStart":false});
            var Q9;
            Q9=makeQuery(id+"F19.opExtrude","CAP_EDGE",EDGE,{"disambiguationData":[OSD([sQuery(id+"F0.wireOp",EDGE,"E27")])],"isStart":false});
            var Q10;
            Q10=makeQuery(id+"F19.opExtrude","CAP_EDGE",EDGE,{"disambiguationData":[OSD([sQuery(id+"F0.wireOp",EDGE,"E29")])],"isStart":false});
            var Q11;
            Q11=makeQuery(id+"F19.opExtrude","CAP_EDGE",EDGE,{"disambiguationData":[OSD([sQuery(id+"F0.wireOp",EDGE,"E28")])],"isStart":false});
            var Q12;
            Q12=makeQuery(id+"F19.opExtrude","CAP_EDGE",EDGE,{"disambiguationData":[OSD([sQuery(id+"F0.wireOp",EDGE,"E32.0")])],"isStart":false});
            var Q13;
            Q13=makeQuery(id+"F19.opExtrude","CAP_EDGE",EDGE,{"disambiguationData":[OSD([sQuery(id+"F0.wireOp",EDGE,"E33.0")])],"isStart":false});
            var Q14;
            Q14=makeQuery(id+"F19.opExtrude","CAP_EDGE",EDGE,{"disambiguationData":[OSD([sQuery(id+"F0.wireOp",EDGE,"E34.0")])],"isStart":false});
            var Q15;
            Q15=makeQuery(id+"F19.opExtrude","CAP_EDGE",EDGE,{"disambiguationData":[OSD([sQuery(id+"F0.wireOp",EDGE,"E35.0")])],"isStart":false});
            fillet(context, id + "F27", {"entities" : qUnion([Q0, Q1, Q2, Q3, Q4, Q5, Q6, Q7, Q8, Q9, Q10, Q11, Q12, Q13, Q14, Q15]), "radius" : 5 * mm, "tangentPropagation" : true, "allowEdgeOverflow" : false});
        }
        {
            var Q0;
            Q0=makeQuery(id+"F1.opExtrude","SWEPT_BODY",BODY,{"disambiguationData":[OSD([sQuery(id+"F0.wireOp",EDGE,"E0.bottom"),sQuery(id+"F0.wireOp",EDGE,"E0.top"),sQuery(id+"F0.wireOp",EDGE,"E0.right"),sQuery(id+"F0.wireOp",EDGE,"E6"),sQuery(id+"F0.wireOp",EDGE,"E7"),sQuery(id+"F0.wireOp",EDGE,"gIGV9JjZ-nNWi-Sog9-6HsN-JS0wgbCRWOlJ")])]});
            transform(context, id + "F28", {"entities" : qUnion([Q0]), "transformType" : TransformType.TRANSLATION_3D, "dx" : 0 * mm, "dy" : 0 * mm, "dz" : 72.1 * mm, "makeCopy" : true});
        }
        {
            var Q0;
            Q0=makeQuery(id+"F28.opPattern","COPY",BODY,{"derivedFrom":makeQuery(id+"F1.opExtrude","SWEPT_BODY",BODY,{"disambiguationData":[OSD([sQuery(id+"F0.wireOp",EDGE,"E0.bottom"),sQuery(id+"F0.wireOp",EDGE,"E0.top"),sQuery(id+"F0.wireOp",EDGE,"E0.right"),sQuery(id+"F0.wireOp",EDGE,"E6"),sQuery(id+"F0.wireOp",EDGE,"E7"),sQuery(id+"F0.wireOp",EDGE,"gIGV9JjZ-nNWi-Sog9-6HsN-JS0wgbCRWOlJ")])]}),"instanceName":"1"});
            deleteBodies(context, id + "F29", {"entities" : qUnion([Q0])});
        }
        {
            var Q0;
            {var subQ0=sQuery(id+"F0.wireOp",EDGE,"E6");Q0=makeQuery(id+"F2.boolean.opBoolean","MERGE",FACE,{"derivedFrom":[makeQuery(id+"F1.opExtrude","CAP_FACE",FACE,{"disambiguationData":[OSD([sQuery(id+"F0.wireOp",EDGE,"E0.bottom"),sQuery(id+"F0.wireOp",EDGE,"E0.top"),sQuery(id+"F0.wireOp",EDGE,"E0.right"),subQ0,sQuery(id+"F0.wireOp",EDGE,"E7"),sQuery(id+"F0.wireOp",EDGE,"gIGV9JjZ-nNWi-Sog9-6HsN-JS0wgbCRWOlJ")])],"isStart":false}),makeQuery(id+"F2.opExtrude","CAP_FACE",FACE,{"disambiguationData":[OSD([sQuery(id+"F0.wireOp",EDGE,"E4"),subQ0])],"isStart":false})]});}
            var sketch = newSketch(context, id + "F30", { "sketchPlane" : qUnion([Q0])});
            skLineSegment(sketch, "E100.0", {"start": v(37, 20.25) * mm, "end": v(25, 20.25) * mm, "construction": true});
            skLineSegment(sketch, "E101.0", {"start": v(37, 20.75) * mm, "end": v(25, 20.75) * mm, "construction": true});
            skLineSegment(sketch, "E102.0", {"start": v(37, 19.75) * mm, "end": v(25, 19.75) * mm, "construction": true});
            skLineSegment(sketch, "E103.0", {"start": v(31.5, 0) * mm, "end": v(31.5, 26) * mm, "construction": true});
            skLineSegment(sketch, "E104.0", {"start": v(35.2, -0.25) * mm, "end": v(35.2, 25.75) * mm, "construction": true});
            skLineSegment(sketch, "E105.0", {"start": v(37, 21.55) * mm, "end": v(25, 21.55) * mm, "construction": true});
            skLineSegment(sketch, "E106.0", {"start": v(34, -0.25) * mm, "end": v(34, 25.75) * mm, "construction": true});
            skLineSegment(sketch, "E107", {"start": v(31.5, 16.25) * mm, "end": v(31.5, 17.5) * mm, "construction": true});
            skLineSegment(sketch, "E108", {"start": v(35.2, 20.25) * mm, "end": v(34, 21.55) * mm});
            skLineSegment(sketch, "E109", {"start": v(34, 21.55) * mm, "end": v(34.51, 22.02) * mm});
            skLineSegment(sketch, "E110", {"start": v(34.51, 22.02) * mm, "end": v(36.15, 20.25) * mm});
            skLineSegment(sketch, "E111.MirrorCS", {"start": v(34.51, 18.48) * mm, "end": v(36.15, 20.25) * mm});
            skLineSegment(sketch, "E112.MirrorCS", {"start": v(35.2, 20.25) * mm, "end": v(34, 18.95) * mm});
            skLineSegment(sketch, "E113.MirrorCS", {"start": v(34, 18.95) * mm, "end": v(34.51, 18.48) * mm});
            skLineSegment(sketch, "E114.MirrorCS", {"start": v(27.8, 20.25) * mm, "end": v(29, 21.55) * mm});
            skLineSegment(sketch, "E115.MirrorCS", {"start": v(29, 21.55) * mm, "end": v(28.49, 22.02) * mm});
            skLineSegment(sketch, "E116.MirrorCS", {"start": v(28.49, 22.02) * mm, "end": v(26.85, 20.25) * mm});
            skLineSegment(sketch, "E117.MirrorCS", {"start": v(28.49, 18.48) * mm, "end": v(26.85, 20.25) * mm});
            skLineSegment(sketch, "E118.MirrorCS", {"start": v(27.8, 20.25) * mm, "end": v(29, 18.95) * mm});
            skLineSegment(sketch, "E119.MirrorCS", {"start": v(29, 18.95) * mm, "end": v(28.49, 18.48) * mm});
            skLineSegment(sketch, "E120", {"start": v(34.74, 20.75) * mm, "end": v(28.26, 20.75) * mm});
            skLineSegment(sketch, "E121", {"start": v(34.74, 19.75) * mm, "end": v(28.26, 19.75) * mm});
            skLineSegment(sketch, "E122", {"start": v(34.51, 22.02) * mm, "end": v(34, 22.58) * mm});
            skSolve(sketch);
        }
        {
            var Q0;
            {var subQ0=sQuery(id+"F30.wireOp",EDGE,"E109");Q0=makeQuery(id+"F30.imprint","IMPRINT",FACE,{"disambiguationData":[TD([[makeQuery(id+"F30.imprint","IMPRINT",EDGE,{"derivedFrom":subQ0}),-1.0]])]});}
            var Q1;
            {var subQ4=sQuery(id+"F30.wireOp",EDGE,"E120");Q1=makeQuery(id+"F30.imprint","IMPRINT",FACE,{"disambiguationData":[TD([[makeQuery(id+"F30.imprint","IMPRINT",EDGE,{"derivedFrom":subQ4}),1.0]])]});}
            var Q2;
            {var subQ0=sQuery(id+"F30.wireOp",EDGE,"E115.MirrorCS");Q2=makeQuery(id+"F30.imprint","IMPRINT",FACE,{"disambiguationData":[TD([[makeQuery(id+"F30.imprint","IMPRINT",EDGE,{"derivedFrom":subQ0}),1.0]])]});}
            extrude(context, id + "F31", {"entities" : qUnion([Q0, Q1, Q2]), "operationType" : NewBodyOperationType.REMOVE, "oppositeDirection" : true, "depth" : 1 * mm});
        }
        {
            var Q0;
            Q0=makeQuery(id+"F0.imprint","IMPRINT",FACE,{"disambiguationData":[TD([[makeQuery(id+"F0.imprint","IMPRINT",EDGE,{"derivedFrom":sQuery(id+"F0.wireOp",EDGE,"E23")}),-1.0]])]});
            extrude(context, id + "F32", {"entities" : qUnion([Q0]), "operationType" : NewBodyOperationType.ADD, "depth" : 9.5 * mm});
        }
        {
            var Q0;
            {var subQ0=sQuery(id+"F0.wireOp",EDGE,"E48.MirrorCS");Q0=makeQuery(id+"F0.imprint","IMPRINT",FACE,{"disambiguationData":[TD([[makeQuery(id+"F0.imprint","IMPRINT",EDGE,{"derivedFrom":subQ0}),1.0]])]});}
            var Q1;
            {var subQ4=sQuery(id+"F0.wireOp",EDGE,"E43");Q1=makeQuery(id+"F0.imprint","IMPRINT",FACE,{"disambiguationData":[TD([[makeQuery(id+"F0.imprint","IMPRINT",EDGE,{"derivedFrom":subQ4}),-1.0]])]});}
            extrude(context, id + "F33", {"entities" : qUnion([Q0, Q1]), "operationType" : NewBodyOperationType.ADD, "depth" : 6 * mm});
        }
        {
            var Q0;
            {var subQ0=sQuery(id+"F0.wireOp",EDGE,"E40");Q0=makeQuery(id+"F0.imprint","IMPRINT",FACE,{"disambiguationData":[TD([[makeQuery(id+"F0.imprint","IMPRINT",EDGE,{"derivedFrom":subQ0}),-1.0]])]});}
            var Q1;
            {var subQ2=sQuery(id+"F0.wireOp",EDGE,"E23");Q1=makeQuery(id+"F0.imprint","IMPRINT",FACE,{"disambiguationData":[TD([[makeQuery(id+"F0.imprint","IMPRINT",EDGE,{"derivedFrom":subQ2}),1.0]])]});}
            var Q2;
            {var subQ0=sQuery(id+"F0.wireOp",EDGE,"E46.MirrorCS");Q2=makeQuery(id+"F0.imprint","IMPRINT",FACE,{"disambiguationData":[TD([[makeQuery(id+"F0.imprint","IMPRINT",EDGE,{"derivedFrom":subQ0}),1.0]])]});}
            extrude(context, id + "F34", {"entities" : qUnion([Q0, Q1, Q2]), "operationType" : NewBodyOperationType.ADD, "depth" : 1.8 * mm});
        }
        {
            var Q0;
            {var subQ0=sQuery(id+"F0.wireOp",EDGE,"E48.MirrorCS");Q0=makeQuery(id+"F0.imprint","IMPRINT",FACE,{"disambiguationData":[TD([[makeQuery(id+"F0.imprint","IMPRINT",EDGE,{"derivedFrom":subQ0}),-1.0]])]});}
            var Q1;
            {var subQ4=sQuery(id+"F0.wireOp",EDGE,"E44");Q1=makeQuery(id+"F0.imprint","IMPRINT",FACE,{"disambiguationData":[TD([[makeQuery(id+"F0.imprint","IMPRINT",EDGE,{"derivedFrom":subQ4}),1.0]])]});}
            extrude(context, id + "F35", {"entities" : qUnion([Q0, Q1]), "operationType" : NewBodyOperationType.ADD, "depth" : 1.8 * mm});
        }
        {
            var Q0;
            Q0=makeQuery(id+"F32.opExtrude","SWEPT_FACE",FACE,{"disambiguationData":[OSD([sQuery(id+"F0.wireOp",EDGE,"E46.MirrorCS")])]});
            extrude(context, id + "F36", {"entities" : qUnion([Q0]), "operationType" : NewBodyOperationType.REMOVE, "oppositeDirection" : true, "depth" : 0.65 * mm});
        }
        {
            var Q0;
            Q0=makeQuery(id+"F32.opExtrude","SWEPT_FACE",FACE,{"disambiguationData":[OSD([sQuery(id+"F0.wireOp",EDGE,"E42")])]});
            extrude(context, id + "F37", {"entities" : qUnion([Q0]), "operationType" : NewBodyOperationType.REMOVE, "oppositeDirection" : true, "depth" : 0.65 * mm});
        }
        {
            var Q0;
            {var subQ0=sQuery(id+"F3.wireOp",EDGE,"E64.0");Q0=makeQuery(id+"F8.boolean.opBoolean","MERGE",FACE,{"derivedFrom":[makeQuery(id+"F6.opExtrude","CAP_FACE",FACE,{"disambiguationData":[OSD([sQuery(id+"F3.wireOp",EDGE,"E62.0"),sQuery(id+"F3.wireOp",EDGE,"E63.0"),subQ0,sQuery(id+"F5.wireOp",EDGE,"E65.0")])],"isStart":false}),makeQuery(id+"F8.opExtrude","SWEPT_FACE",FACE,{"disambiguationData":[OSD([subQ0])]})]});}
            var sketch = newSketch(context, id + "F38", { "sketchPlane" : qUnion([Q0])});
            skLineSegment(sketch, "E123.0", {"start": v(-2, 2) * mm, "end": v(-2, 24) * mm});
            skSolve(sketch);
        }
        {
            var Q0;
            {var subQ0=sQuery(id+"F38.wireOp",EDGE,"E123.0");Q0=makeQuery(id+"F38.imprint","IMPRINT",FACE,{"disambiguationData":[TD([[makeQuery(id+"F38.imprint","IMPRINT",EDGE,{"derivedFrom":subQ0}),-1.0]])]});}
            extrude(context, id + "F39", {"entities" : qUnion([Q0]), "operationType" : NewBodyOperationType.ADD, "depth" : 5 * mm});
        }
        {
            var Q0;
            {var subQ0=sQuery(id+"F0.wireOp",EDGE,"E0.top");Q0=makeQuery(id+"F11.boolean.opBoolean","MERGE",EDGE,{"derivedFrom":[makeQuery(id+"F8.opExtrude","CAP_EDGE",EDGE,{"disambiguationData":[OSD([subQ0,sQuery(id+"F0.wireOp",EDGE,"E59.0")])],"isStart":false}),makeQuery(id+"F11.opExtrude","SWEPT_EDGE",EDGE,{"disambiguationData":[OSD([subQ0,sQuery(id+"F0.wireOp",EDGE,"E0.left")])]})]});}
            var Q1;
            {var subQ0=sQuery(id+"F0.wireOp",EDGE,"E0.bottom");Q1=makeQuery(id+"F11.boolean.opBoolean","MERGE",EDGE,{"derivedFrom":[makeQuery(id+"F8.opExtrude","CAP_EDGE",EDGE,{"disambiguationData":[OSD([subQ0,sQuery(id+"F0.wireOp",EDGE,"E59.0")])],"isStart":false}),makeQuery(id+"F11.opExtrude","SWEPT_EDGE",EDGE,{"disambiguationData":[OSD([subQ0,sQuery(id+"F0.wireOp",EDGE,"E0.left")])]})]});}
            fillet(context, id + "F40", {"entities" : qUnion([Q0, Q1]), "radius" : 5 * mm, "tangentPropagation" : true, "allowEdgeOverflow" : false});
        }
        {
            var Q0;
            Q0=makeQuery(id+"F8.opExtrude","CAP_EDGE",EDGE,{"disambiguationData":[OSD([sQuery(id+"F7.wireOp",EDGE,"E68.0"),sQuery(id+"F7.wireOp",EDGE,"E68.1"),sQuery(id+"F7.wireOp",EDGE,"E68.2")])],"isStart":false});
            var Q1;
            {var subQ0=sQuery(id+"F0.wireOp",EDGE,"E0.top");Q1=makeQuery(id+"F40.opFillet","BLEND_EDGE",EDGE,{"blendedFrom":[makeQuery(id+"F11.boolean.opBoolean","MERGE",EDGE,{"derivedFrom":[makeQuery(id+"F8.opExtrude","CAP_EDGE",EDGE,{"disambiguationData":[OSD([subQ0,sQuery(id+"F0.wireOp",EDGE,"E59.0")])],"isStart":false}),makeQuery(id+"F11.opExtrude","SWEPT_EDGE",EDGE,{"disambiguationData":[OSD([subQ0,sQuery(id+"F0.wireOp",EDGE,"E0.left")])]})]}),makeQuery(id+"F8.opExtrude","SWEPT_FACE",FACE,{"disambiguationData":[OSD([sQuery(id+"F7.wireOp",EDGE,"E68.0"),sQuery(id+"F7.wireOp",EDGE,"E68.1"),sQuery(id+"F7.wireOp",EDGE,"E68.2")])]})],"blendedInto":[makeQuery(id+"F8.opExtrude","SWEPT_FACE",FACE,{"disambiguationData":[OSD([sQuery(id+"F7.wireOp",EDGE,"E68.0"),sQuery(id+"F7.wireOp",EDGE,"E68.1"),sQuery(id+"F7.wireOp",EDGE,"E68.2")])]})]});}
            var Q2;
            Q2=makeQuery(id+"F8.opExtrude","SWEPT_EDGE",EDGE,{"disambiguationData":[OSD([sQuery(id+"F0.wireOp",EDGE,"E0.top"),sQuery(id+"F0.wireOp",EDGE,"E59.0"),sQuery(id+"F7.wireOp",EDGE,"E68.0")])]});
            var Q3;
            Q3=makeQuery(id+"F1.opExtrude","CAP_EDGE",EDGE,{"disambiguationData":[OSD([sQuery(id+"F0.wireOp",EDGE,"E59.0")])],"isStart":false});
            var Q4;
            Q4=makeQuery(id+"F1.opExtrude","SWEPT_EDGE",EDGE,{"disambiguationData":[OSD([sQuery(id+"F0.wireOp",EDGE,"E0.top"),sQuery(id+"F0.wireOp",EDGE,"E59.0")])]});
            var Q5;
            Q5=makeQuery(id+"F1.opExtrude","CAP_EDGE",EDGE,{"disambiguationData":[OSD([sQuery(id+"F0.wireOp",EDGE,"E0.bottom")])],"isStart":false});
            var Q6;
            Q6=makeQuery(id+"F1.opExtrude","CAP_EDGE",EDGE,{"disambiguationData":[OSD([sQuery(id+"F0.wireOp",EDGE,"E0.right")])],"isStart":false});
            var Q7;
            Q7=makeQuery(id+"F1.opExtrude","CAP_EDGE",EDGE,{"disambiguationData":[OSD([sQuery(id+"F0.wireOp",EDGE,"E0.top")])],"isStart":false});
            var Q8;
            {var subQ0=sQuery(id+"F0.wireOp",EDGE,"E0.right");var subQ1=sQuery(id+"F0.wireOp",EDGE,"E0.top");Q8=makeQuery(id+"F11.boolean.opBoolean","MERGE",EDGE,{"derivedFrom":[makeQuery(id+"F1.opExtrude","SWEPT_EDGE",EDGE,{"disambiguationData":[OSD([subQ1,subQ0])]}),makeQuery(id+"F11.opExtrude","SWEPT_EDGE",EDGE,{"disambiguationData":[OSD([subQ1,subQ0])]})]});}
            var Q9;
            Q9=makeQuery(id+"F8.opExtrude","SWEPT_EDGE",EDGE,{"disambiguationData":[OSD([sQuery(id+"F0.wireOp",EDGE,"E0.bottom"),sQuery(id+"F0.wireOp",EDGE,"E59.0"),sQuery(id+"F7.wireOp",EDGE,"E68.2")])]});
            var Q10;
            {var subQ0=sQuery(id+"F0.wireOp",EDGE,"E0.bottom");Q10=makeQuery(id+"F40.opFillet","BLEND_EDGE",EDGE,{"blendedFrom":[makeQuery(id+"F11.boolean.opBoolean","MERGE",EDGE,{"derivedFrom":[makeQuery(id+"F8.opExtrude","CAP_EDGE",EDGE,{"disambiguationData":[OSD([subQ0,sQuery(id+"F0.wireOp",EDGE,"E59.0")])],"isStart":false}),makeQuery(id+"F11.opExtrude","SWEPT_EDGE",EDGE,{"disambiguationData":[OSD([subQ0,sQuery(id+"F0.wireOp",EDGE,"E0.left")])]})]}),makeQuery(id+"F8.opExtrude","SWEPT_FACE",FACE,{"disambiguationData":[OSD([sQuery(id+"F7.wireOp",EDGE,"E68.0"),sQuery(id+"F7.wireOp",EDGE,"E68.1"),sQuery(id+"F7.wireOp",EDGE,"E68.2")])]})],"blendedInto":[makeQuery(id+"F8.opExtrude","SWEPT_FACE",FACE,{"disambiguationData":[OSD([sQuery(id+"F7.wireOp",EDGE,"E68.0"),sQuery(id+"F7.wireOp",EDGE,"E68.1"),sQuery(id+"F7.wireOp",EDGE,"E68.2")])]})]});}
            var Q11;
            Q11=makeQuery(id+"F1.opExtrude","SWEPT_EDGE",EDGE,{"disambiguationData":[OSD([sQuery(id+"F0.wireOp",EDGE,"E0.bottom"),sQuery(id+"F0.wireOp",EDGE,"E59.0")])]});
            var Q12;
            {var subQ0=sQuery(id+"F0.wireOp",EDGE,"E0.right");var subQ1=sQuery(id+"F0.wireOp",EDGE,"E0.bottom");Q12=makeQuery(id+"F11.boolean.opBoolean","MERGE",EDGE,{"derivedFrom":[makeQuery(id+"F1.opExtrude","SWEPT_EDGE",EDGE,{"disambiguationData":[OSD([subQ1,subQ0])]}),makeQuery(id+"F11.opExtrude","SWEPT_EDGE",EDGE,{"disambiguationData":[OSD([subQ1,subQ0])]})]});}
            fillet(context, id + "F41", {"entities" : qUnion([Q0, Q1, Q2, Q3, Q4, Q5, Q6, Q7, Q8, Q9, Q10, Q11, Q12]), "radius" : 3 * mm, "tangentPropagation" : true, "allowEdgeOverflow" : false});
        }
        {
            var Q0;
            {var subQ0=sQuery(id+"F0.wireOp",EDGE,"E6");Q0=makeQuery(id+"F2.boolean.opBoolean","MERGE",FACE,{"derivedFrom":[makeQuery(id+"F1.opExtrude","CAP_FACE",FACE,{"disambiguationData":[OSD([sQuery(id+"F0.wireOp",EDGE,"E0.bottom"),sQuery(id+"F0.wireOp",EDGE,"E0.top"),sQuery(id+"F0.wireOp",EDGE,"E0.right"),subQ0,sQuery(id+"F0.wireOp",EDGE,"E59.0")])],"isStart":false}),makeQuery(id+"F2.opExtrude","CAP_FACE",FACE,{"disambiguationData":[OSD([sQuery(id+"F0.wireOp",EDGE,"E4"),subQ0])],"isStart":false})]});}
            var sketch = newSketch(context, id + "F42", { "sketchPlane" : qUnion([Q0])});
            skLineSegment(sketch, "E124", {"start": v(38, 3) * mm, "end": v(36.5, 3) * mm, "construction": true});
            skLineSegment(sketch, "E125", {"start": v(36.5, 3) * mm, "end": v(36.5, 4.5) * mm});
            skCircle(sketch, "E126", {"center": v(36.5, 4.5) * mm, "radius": 1.5 * mm});
            skSolve(sketch);
        }
        {
            var Q0;
            {var subQ0=sQuery(id+"F0.wireOp",EDGE,"E0.bottom");Q0=makeQuery(id+"F11.boolean.opBoolean","MERGE",FACE,{"derivedFrom":[makeQuery(id+"F8.boolean.opBoolean","MERGE",FACE,{"derivedFrom":[makeQuery(id+"F1.opExtrude","SWEPT_FACE",FACE,{"disambiguationData":[OSD([subQ0])]}),makeQuery(id+"F8.opExtrude","SWEPT_FACE",FACE,{"disambiguationData":[OSD([subQ0,sQuery(id+"F0.wireOp",EDGE,"E59.0")])]})]}),makeQuery(id+"F11.opExtrude","SWEPT_FACE",FACE,{"disambiguationData":[OSD([subQ0])]})]});}
            var sketch = newSketch(context, id + "F43", { "sketchPlane" : qUnion([Q0])});
            skLineSegment(sketch, "E127", {"start": v(38, 10.5) * mm, "end": v(36.5, 10.5) * mm, "construction": true});
            skLineSegment(sketch, "E128", {"start": v(36.5, 10.5) * mm, "end": v(36.5, 9) * mm, "construction": true});
            skCircle(sketch, "E129", {"center": v(36.5, 9) * mm, "radius": 1.5 * mm});
            skSolve(sketch);
        }
        {
            var Q0;
            Q0 = qSketchRegion(id + "F43", true);
            extrude(context, id + "F44", {"entities" : qUnion([Q0]), "operationType" : NewBodyOperationType.REMOVE, "oppositeDirection" : true, "depth" : 3 * mm});
        }
        {
            var Q0;
            Q0 = qSketchRegion(id + "F42", true);
            extrude(context, id + "F45", {"entities" : qUnion([Q0]), "operationType" : NewBodyOperationType.REMOVE, "oppositeDirection" : true, "depth" : 3.25 * mm});
        }
        {
            var Q0;
            Q0 = qSketchRegion(id + "F43", true);
            extrude(context, id + "F46", {"entities" : qUnion([Q0]), "operationType" : NewBodyOperationType.REMOVE, "oppositeDirection" : true, "depth" : 1 * mm});
        }
        {
            var Q0;
            Q0=makeQuery(id+"F18.opExtrude","SWEPT_BODY",BODY,{"disambiguationData":[OSD([sQuery(id+"F0.wireOp",EDGE,"E9"),sQuery(id+"F0.wireOp",EDGE,"E10"),sQuery(id+"F0.wireOp",EDGE,"E11"),sQuery(id+"F0.wireOp",EDGE,"E12"),sQuery(id+"F0.wireOp",EDGE,"E14.0"),sQuery(id+"F0.wireOp",EDGE,"E15.0"),sQuery(id+"F0.wireOp",EDGE,"E16.0"),sQuery(id+"F0.wireOp",EDGE,"E17.0"),sQuery(id+"F0.wireOp",EDGE,"E22"),sQuery(id+"F0.wireOp",EDGE,"E24"),sQuery(id+"F0.wireOp",EDGE,"E25.MirrorCS"),sQuery(id+"F0.wireOp",EDGE,"E32.0"),sQuery(id+"F0.wireOp",EDGE,"E33.0"),sQuery(id+"F0.wireOp",EDGE,"E34.0"),sQuery(id+"F0.wireOp",EDGE,"E35.0"),sQuery(id+"F0.wireOp",EDGE,"E38"),sQuery(id+"F0.wireOp",EDGE,"E39")])]});
            transform(context, id + "F47", {"entities" : qUnion([Q0]), "transformType" : TransformType.TRANSLATION_3D, "dx" : 0 * mm, "dy" : 0 * mm, "dz" : -34.7 * mm, "makeCopy" : true});
        }
        {
            var Q0;
            Q0=makeQuery(id+"F1.opExtrude","SWEPT_BODY",BODY,{"disambiguationData":[OSD([sQuery(id+"F0.wireOp",EDGE,"E0.bottom"),sQuery(id+"F0.wireOp",EDGE,"E0.top"),sQuery(id+"F0.wireOp",EDGE,"E0.right"),sQuery(id+"F0.wireOp",EDGE,"E6"),sQuery(id+"F0.wireOp",EDGE,"E59.0")])]});
            transform(context, id + "F48", {"entities" : qUnion([Q0]), "transformType" : TransformType.TRANSLATION_3D, "dx" : -68.8 * mm, "dy" : 0 * mm, "dz" : 0 * mm, "makeCopy" : true});
        }
    });
